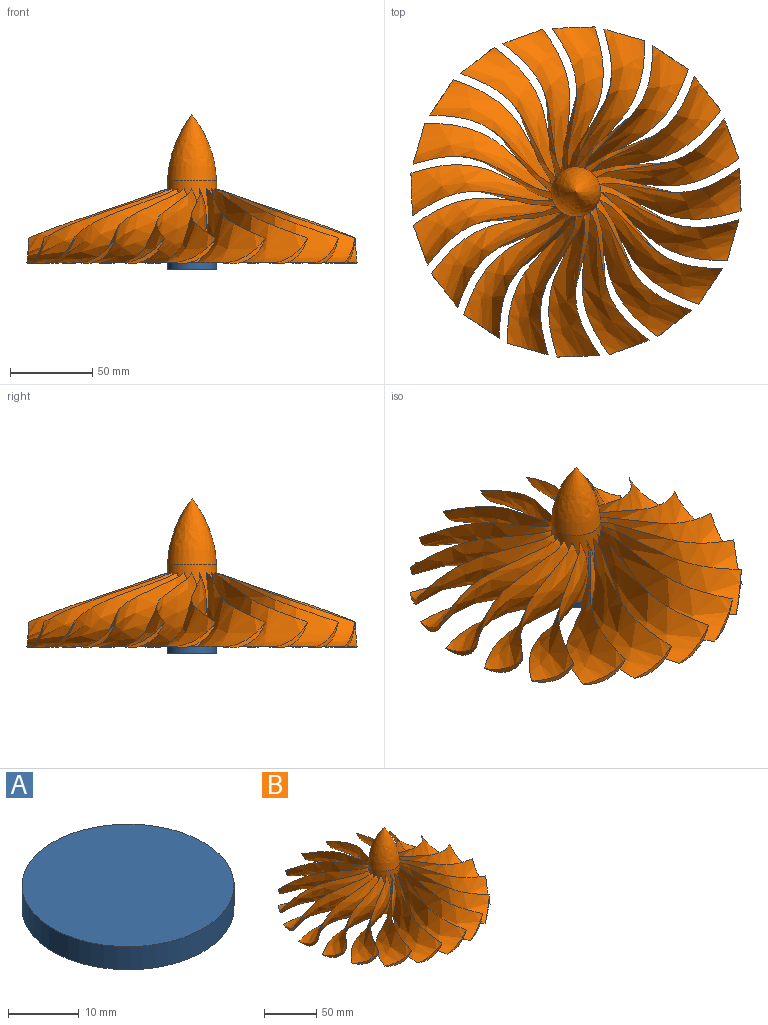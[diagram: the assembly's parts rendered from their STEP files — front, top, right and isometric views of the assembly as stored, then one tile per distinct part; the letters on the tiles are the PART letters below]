
ASSEMBLY  parts=2 mates=1
PART A: 3 faces, bbox 30x30x4 mm
  f0: cylinder r=15mm len=30mm, axis (0,0,1), area 377mm2, adj f1,f2
  f1: plane 30x30mm, normal (0,0,-1), area 706.9mm2, adj f0
  f2: plane 30x30mm, normal (0,0,1), area 706.9mm2, adj f0
PART B: 65 faces, bbox 200x200x90.6 mm
  f0: cylinder r=15mm len=50mm, axis (0,0,-1), area 2604mm2, adj f1,f2,f3,f4,f5,f7,f8,f10
  f1: cylinder r=15mm len=24.05mm, axis (0,0,-1), area 13.4mm2, adj f0,f20
  f2: cylinder r=15mm len=7.16mm, axis (0,0,-1), area 15.1mm2, adj f0,f3,f19
  f3: plane 30x30mm, normal (0,0,-1), area 706.9mm2, adj f0,f2
  f4: bspline ~87.84x49.25mm, area 3372.1mm2, adj f0,f5,f6
  f5: bspline ~86.37x46.01mm, area 3168.4mm2, adj f0,f4,f6
  f6: plane 24.71x15.57mm, normal (-0.31,-0.95,0), area 53.5mm2, adj f4,f5
  f7: bspline ~78.1x70.35mm, area 3372.1mm2, adj f0,f8,f9
  f8: bspline ~83.93x71.69mm, area 3168.4mm2, adj f0,f7,f9
  f9: plane 21.02x15.57mm, normal (-0.59,-0.81,0), area 53.5mm2, adj f7,f8
  f10: bspline ~93.66x67.66mm, area 3372.1mm2, adj f0,f11,f12
  f11: bspline ~81.64x59.8mm, area 3168.4mm2, adj f0,f10,f12
  f12: plane 21.02x15.57mm, normal (-0.81,-0.59,0), area 53.5mm2, adj f10,f11
  f13: bspline ~90.51x46.3mm, area 3372.1mm2, adj f0,f14,f15
  f14: bspline ~96.94x48.48mm, area 3168.4mm2, adj f0,f13,f15
  f15: plane 24.71x15.57mm, normal (-0.95,-0.31,0), area 53.5mm2, adj f13,f14
  f16: bspline ~100x50.6mm, area 3372.1mm2, adj f0,f17,f18
  f17: bspline ~95.99x48.48mm, area 3168.4mm2, adj f0,f16,f18
  f18: plane 25.98x15.57mm, normal (-1,0,0), area 53.5mm2, adj f16,f17
  f19: bspline ~87.84x49.25mm, area 3372.3mm2, adj f0,f2,f20,f21
  f20: bspline ~86.37x46.01mm, area 3167.3mm2, adj f0,f1,f19,f21
  f21: plane 24.71x15.57mm, normal (-0.95,0.31,0), area 53.5mm2, adj f19,f20
  f22: bspline ~78.1x70.35mm, area 3372.1mm2, adj f0,f23,f24
  f23: bspline ~83.93x71.69mm, area 3168.4mm2, adj f0,f22,f24
  f24: plane 21.02x15.57mm, normal (-0.81,0.59,0), area 53.5mm2, adj f22,f23
  f25: bspline ~93.66x67.66mm, area 3372.1mm2, adj f0,f26,f27
  f26: bspline ~81.64x59.8mm, area 3168.4mm2, adj f0,f25,f27
  f27: plane 21.02x15.57mm, normal (-0.59,0.81,0), area 53.5mm2, adj f25,f26
  f28: bspline ~90.51x46.3mm, area 3372.1mm2, adj f0,f29,f30
  f29: bspline ~96.94x48.48mm, area 3168.4mm2, adj f0,f28,f30
  f30: plane 24.71x15.57mm, normal (-0.31,0.95,0), area 53.5mm2, adj f28,f29
  f31: bspline ~100x50.6mm, area 3372.1mm2, adj f0,f32,f33
  f32: bspline ~95.99x48.48mm, area 3168.4mm2, adj f0,f31,f33
  f33: plane 25.98x15.57mm, normal (0,1,0), area 53.5mm2, adj f31,f32
  f34: bspline ~87.84x49.25mm, area 3372.1mm2, adj f0,f35,f36
  f35: bspline ~86.37x46.01mm, area 3168.4mm2, adj f0,f34,f36
  f36: plane 24.71x15.57mm, normal (0.31,0.95,0), area 53.5mm2, adj f34,f35
  f37: bspline ~78.1x70.35mm, area 3372.1mm2, adj f0,f38,f39
  f38: bspline ~83.93x71.69mm, area 3168.4mm2, adj f0,f37,f39
  f39: plane 21.02x15.57mm, normal (0.59,0.81,0), area 53.5mm2, adj f37,f38
  f40: bspline ~93.66x67.66mm, area 3372.1mm2, adj f0,f41,f42
  f41: bspline ~81.64x59.8mm, area 3168.4mm2, adj f0,f40,f42
  f42: plane 21.02x15.57mm, normal (0.81,0.59,0), area 53.5mm2, adj f40,f41
  f43: bspline ~90.51x46.3mm, area 3372.1mm2, adj f0,f44,f45
  f44: bspline ~96.94x48.48mm, area 3168.4mm2, adj f0,f43,f45
  f45: plane 24.71x15.57mm, normal (0.95,0.31,0), area 53.5mm2, adj f43,f44
  f46: bspline ~100x50.6mm, area 3372.1mm2, adj f0,f47,f48
  f47: bspline ~95.99x48.48mm, area 3168.4mm2, adj f0,f46,f48
  f48: plane 25.98x15.57mm, normal (1,0,0), area 53.5mm2, adj f46,f47
  f49: bspline ~87.84x49.25mm, area 3372.1mm2, adj f0,f50,f51
  f50: bspline ~86.37x46.01mm, area 3168.4mm2, adj f0,f49,f51
  f51: plane 24.71x15.57mm, normal (0.95,-0.31,0), area 53.5mm2, adj f49,f50
  f52: bspline ~78.1x70.35mm, area 3372.1mm2, adj f0,f53,f54
  f53: bspline ~83.93x71.69mm, area 3168.4mm2, adj f0,f52,f54
  f54: plane 21.02x15.57mm, normal (0.81,-0.59,0), area 53.5mm2, adj f52,f53
  f55: bspline ~93.66x67.66mm, area 3372.1mm2, adj f0,f56,f57
  f56: bspline ~81.64x59.8mm, area 3168.4mm2, adj f0,f55,f57
  f57: plane 21.02x15.57mm, normal (0.59,-0.81,0), area 53.5mm2, adj f55,f56
  f58: bspline ~90.51x46.3mm, area 3372.1mm2, adj f0,f59,f60
  f59: bspline ~96.94x48.48mm, area 3168.4mm2, adj f0,f58,f60
  f60: plane 24.71x15.57mm, normal (0.31,-0.95,0), area 53.5mm2, adj f58,f59
  f61: bspline ~100x50.6mm, area 3372.1mm2, adj f0,f62,f63
  f62: bspline ~95.99x48.48mm, area 3168.4mm2, adj f0,f61,f63
  f63: plane 25.98x15.57mm, normal (0,-1,0), area 53.5mm2, adj f61,f62
  f64: revolved ~40x30mm, area 2613.3mm2, adj f0
PLACE A rot(axis=(0,0,1),20deg) t=(-92.76,-47.39,17.3)mm
PLACE B rot(axis=(0,0,-1),160deg) t=(-92.76,-47.39,17.3)mm
MATE revolute B.f0 <-> A.f0  axis (0,0,1) through (-92.76,-47.39,-7.7)mm
